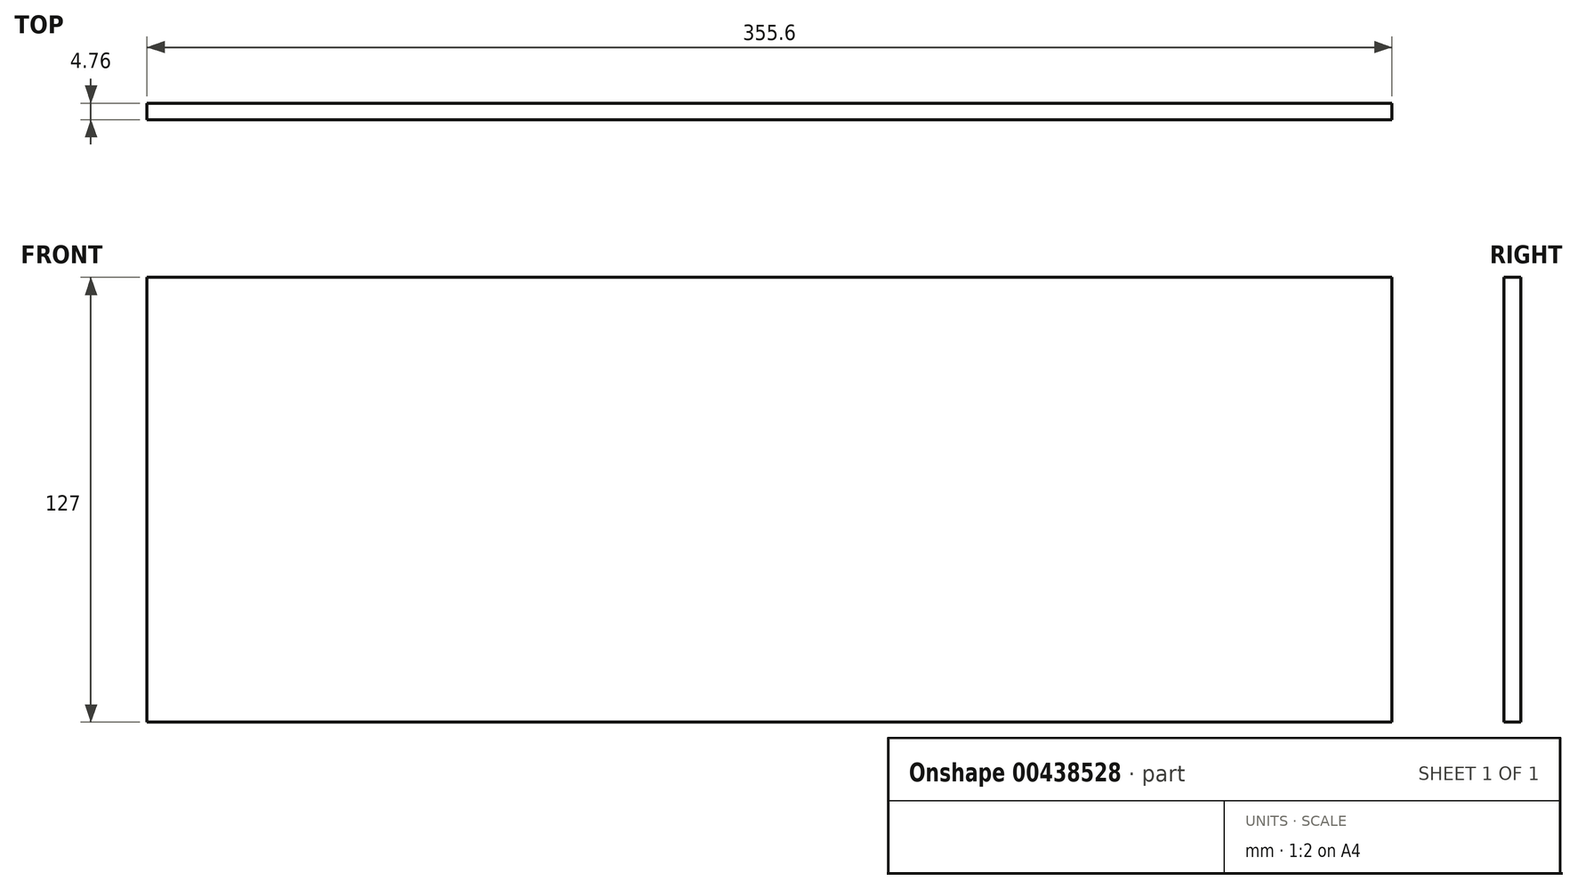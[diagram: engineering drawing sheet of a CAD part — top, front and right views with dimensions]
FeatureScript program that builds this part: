
annotation { "Feature Type Name" : "Feature", "Feature Type Description" : "" }
export const myFeature = defineFeature(function(context is Context, id is Id, definition is map)
    precondition{}
    {
        {
            var Q0;
            Q0=qCreatedBy(makeId("Front.planeOp"),FACE);
            var sketch = newSketch(context, id + "F0", { "sketchPlane" : qUnion([Q0])});
            skLineSegment(sketch, "E0.bottom", {"start": v(-203.99, 9.53) * mm, "end": v(151.61, 9.53) * mm});
            skLineSegment(sketch, "E0.top", {"start": v(-203.99, -117.47) * mm, "end": v(151.61, -117.47) * mm});
            skLineSegment(sketch, "E0.left", {"start": v(-203.99, 9.53) * mm, "end": v(-203.99, -117.47) * mm});
            skLineSegment(sketch, "E0.right", {"start": v(151.61, 9.53) * mm, "end": v(151.61, -117.47) * mm});
            skSolve(sketch);
        }
        {
            var Q0;
            Q0=makeQuery(id+"F0.imprint","IMPRINT",FACE,{"disambiguationData":[TD([[makeQuery(id+"F0.imprint","IMPRINT",EDGE,{"derivedFrom":sQuery(id+"F0.wireOp",EDGE,"E0.bottom")}),-1.0]])]});
            extrude(context, id + "F1", {"entities" : qUnion([Q0]), "depth" : 4.76 * mm});
        }
    });
